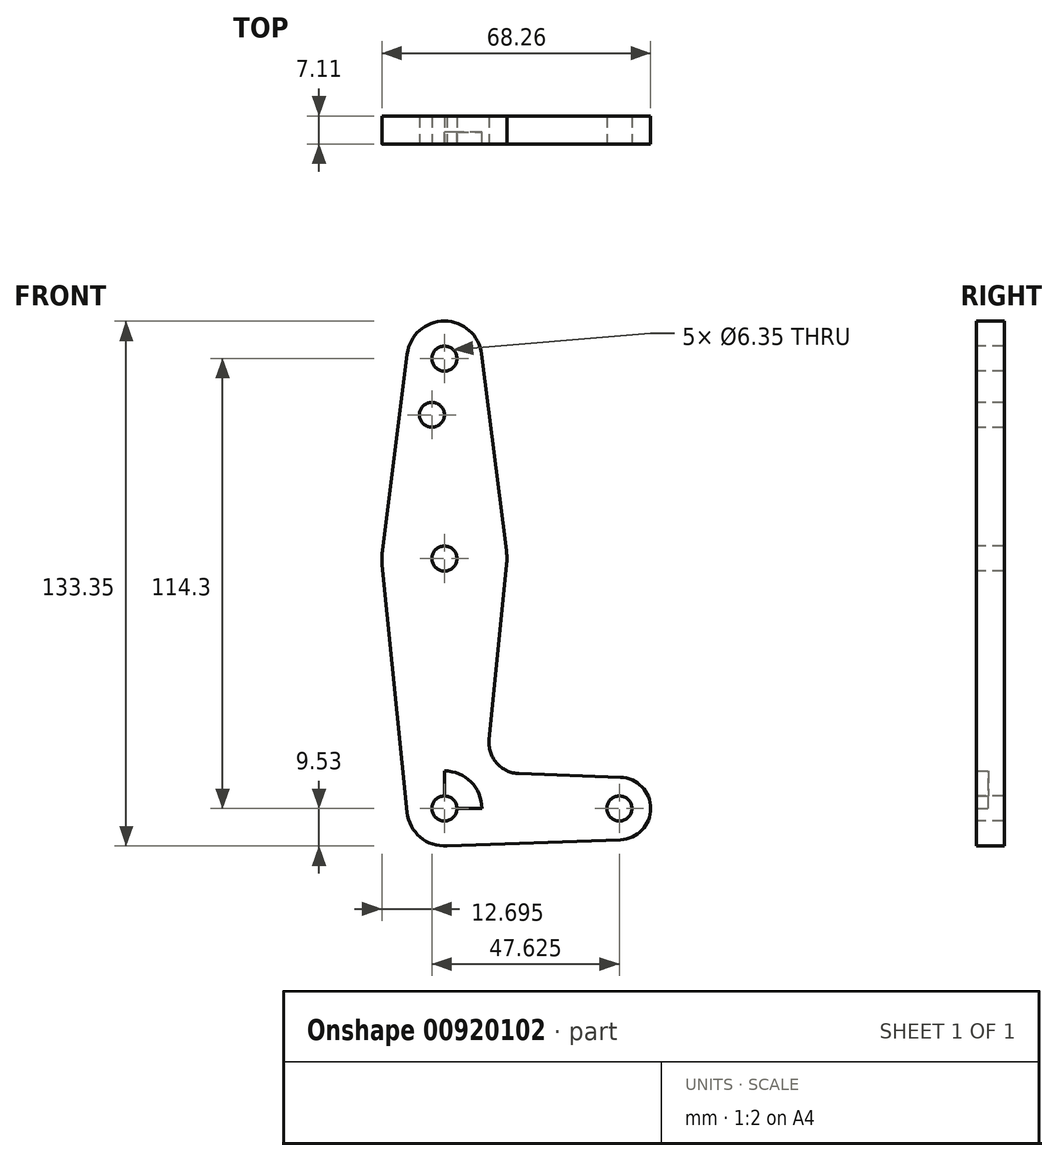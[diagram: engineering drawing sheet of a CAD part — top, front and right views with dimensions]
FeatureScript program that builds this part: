
annotation { "Feature Type Name" : "Feature", "Feature Type Description" : "" }
export const myFeature = defineFeature(function(context is Context, id is Id, definition is map)
    precondition{}
    {
        {
            var Q0;
            Q0=qCreatedBy(makeId("Front.planeOp"),FACE);
            var sketch = newSketch(context, id + "F0", { "sketchPlane" : qUnion([Q0])});
            skCircle(sketch, "E0", {"center": v(0, 0) * mm, "radius": 15.88 * mm});
            skCircle(sketch, "E1", {"center": v(0, 0) * mm, "radius": 3.18 * mm});
            skLineSegment(sketch, "E2", {"start": v(0, 50.8) * mm, "end": v(0, -63.5) * mm});
            skCircle(sketch, "E3", {"center": v(0, 50.8) * mm, "radius": 9.53 * mm});
            skCircle(sketch, "E4", {"center": v(0, 50.8) * mm, "radius": 3.18 * mm});
            skCircle(sketch, "E5", {"center": v(0, -63.5) * mm, "radius": 9.53 * mm});
            skLineSegment(sketch, "E6", {"start": v(0, -63.5) * mm, "end": v(44.45, -63.5) * mm});
            skCircle(sketch, "E7", {"center": v(44.45, -63.5) * mm, "radius": 7.94 * mm});
            skCircle(sketch, "E8", {"center": v(44.45, -63.5) * mm, "radius": 3.18 * mm});
            skLineSegment(sketch, "E9", {"start": v(9.45, 52) * mm, "end": v(15.75, 1.98) * mm});
            skLineSegment(sketch, "E10", {"start": v(-9.45, 52) * mm, "end": v(-15.75, 1.98) * mm});
            skLineSegment(sketch, "E11", {"start": v(-15.8, -1.59) * mm, "end": v(-9.48, -64.45) * mm});
            skLineSegment(sketch, "E12", {"start": v(0, -73.03) * mm, "end": v(44.73, -71.43) * mm});
            skLineSegment(sketch, "E13", {"start": v(15.8, -1.59) * mm, "end": v(11.34, -45.9) * mm});
            skLineSegment(sketch, "E14", {"start": v(44.73, -55.57) * mm, "end": v(18.97, -54.65) * mm});
            skArc(sketch, "E15.filletArc", {"start": v(11.34, -45.9) * mm, "mid": v(13.26, -51.93) * mm, "end": v(18.97, -54.65) * mm});
            skCircle(sketch, "E16", {"center": v(0, -63.5) * mm, "radius": 3.18 * mm});
            skLineSegment(sketch, "E17", {"start": v(0, 0) * mm, "end": v(0, 29.74) * mm});
            skCircle(sketch, "E18", {"center": v(-3.18, 36.53) * mm, "radius": 3.18 * mm});
            skSolve(sketch);
        }
        {
            var Q0;
            Q0 = qSketchRegion(id + "F0", true);
            var Q1;
            {var subQ0=sQuery(id+"F0.wireOp",EDGE,"E5");var subQ1=sQuery(id+"F0.wireOp",EDGE,"E2");var subQ2=makeQuery(id+"F0.imprint","INTERSECT",VERTEX,{"derivedFrom":[subQ1,subQ0]});Q1=makeQuery(id+"F0.imprint","IMPRINT",FACE,{"disambiguationData":[TD([[makeQuery(id+"F0.imprint","IMPRINT",EDGE,{"disambiguationData":[TD([[subQ2,-1.0]])],"derivedFrom":subQ1}),1.0]])]});}
            extrude(context, id + "F1", {"entities" : qUnion([Q0, Q1]), "oppositeDirection" : true, "depth" : 4.06 * mm, "offsetDistance" : 25.4 * mm});
        }
        {
            var Q0;
            Q0 = qSketchRegion(id + "F0", true);
            extrude(context, id + "F2", {"entities" : qUnion([Q0]), "operationType" : NewBodyOperationType.ADD, "depth" : 3.05 * mm, "offsetDistance" : 25.4 * mm});
        }
    });
